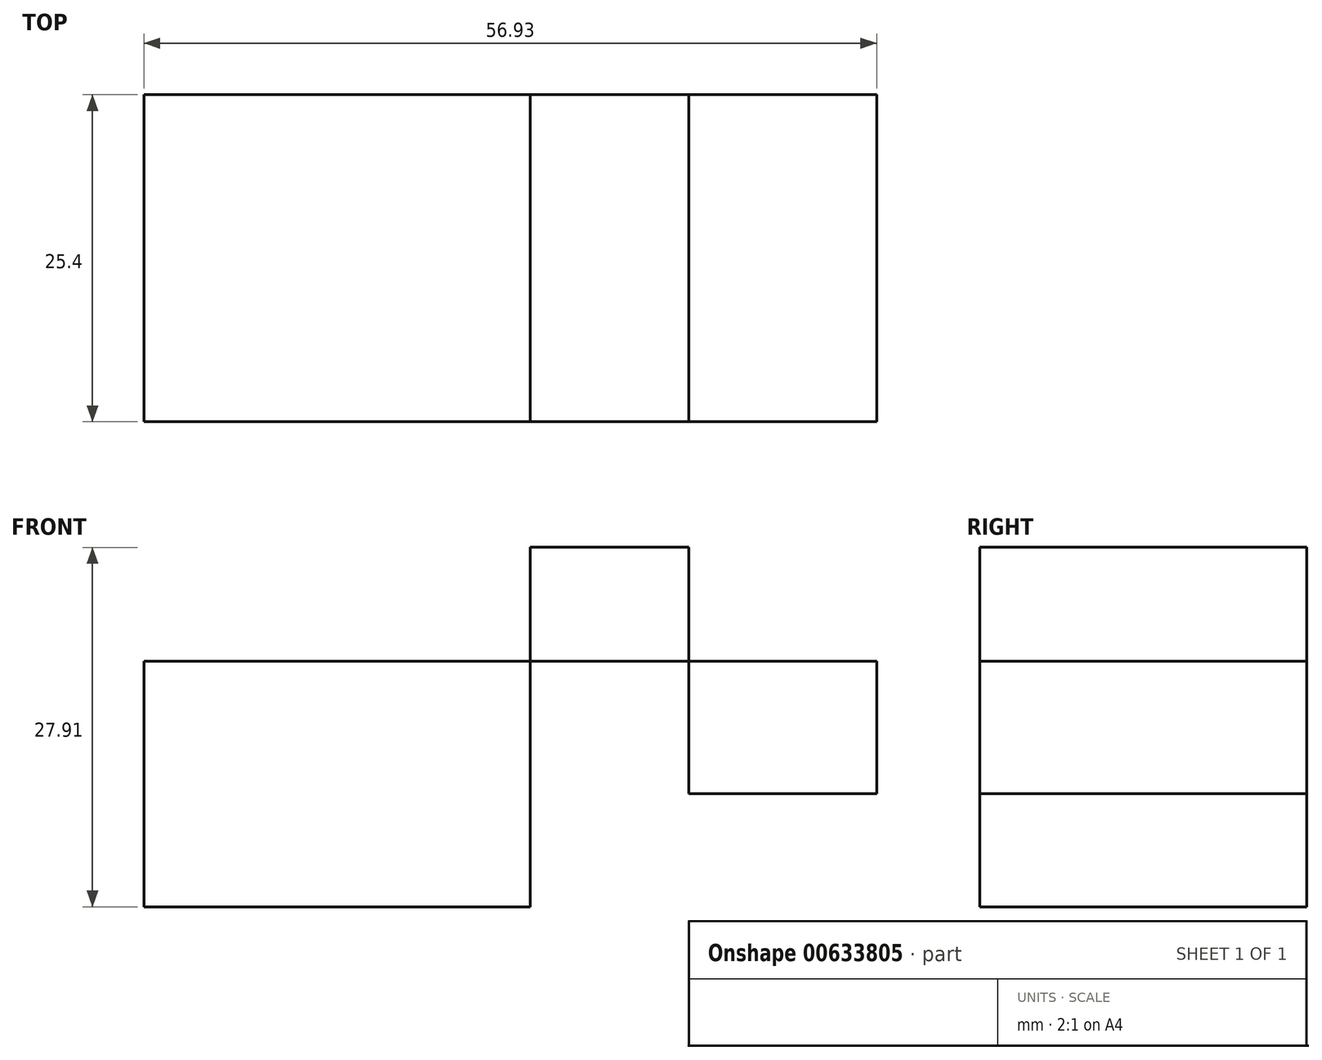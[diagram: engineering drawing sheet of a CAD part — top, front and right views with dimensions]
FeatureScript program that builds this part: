
annotation { "Feature Type Name" : "Feature", "Feature Type Description" : "" }
export const myFeature = defineFeature(function(context is Context, id is Id, definition is map)
    precondition{}
    {
        {
            var Q0;
            Q0=qCreatedBy(makeId("Front.planeOp"),FACE);
            var sketch = newSketch(context, id + "F0", { "sketchPlane" : qUnion([Q0])});
            skLineSegment(sketch, "E0.bottom", {"start": v(-30, 19.08) * mm, "end": v(0, 19.08) * mm});
            skLineSegment(sketch, "E0.top", {"start": v(-30, 0) * mm, "end": v(0, 0) * mm});
            skLineSegment(sketch, "E0.left", {"start": v(-30, 19.08) * mm, "end": v(-30, 0) * mm});
            skLineSegment(sketch, "E0.right", {"start": v(0, 19.08) * mm, "end": v(0, 0) * mm});
            skLineSegment(sketch, "E1.bottom", {"start": v(0, 19.08) * mm, "end": v(12.33, 19.08) * mm});
            skLineSegment(sketch, "E1.top", {"start": v(0, 27.91) * mm, "end": v(12.33, 27.91) * mm});
            skLineSegment(sketch, "E1.left", {"start": v(0, 19.08) * mm, "end": v(0, 27.91) * mm});
            skLineSegment(sketch, "E1.right", {"start": v(12.33, 19.08) * mm, "end": v(12.33, 27.91) * mm});
            skLineSegment(sketch, "E2.bottom", {"start": v(12.33, 19.08) * mm, "end": v(26.93, 19.08) * mm});
            skLineSegment(sketch, "E2.top", {"start": v(12.33, 8.77) * mm, "end": v(26.93, 8.77) * mm});
            skLineSegment(sketch, "E2.left", {"start": v(12.33, 19.08) * mm, "end": v(12.33, 8.77) * mm});
            skLineSegment(sketch, "E2.right", {"start": v(26.93, 19.08) * mm, "end": v(26.93, 8.77) * mm});
            skSolve(sketch);
        }
        {
            var Q0;
            Q0=makeQuery(id+"F0.imprint","IMPRINT",FACE,{"disambiguationData":[TD([[makeQuery(id+"F0.imprint","IMPRINT",EDGE,{"derivedFrom":sQuery(id+"F0.wireOp",EDGE,"E0.bottom")}),-1.0]])]});
            var Q1;
            Q1=makeQuery(id+"F0.imprint","IMPRINT",FACE,{"disambiguationData":[TD([[makeQuery(id+"F0.imprint","IMPRINT",EDGE,{"derivedFrom":sQuery(id+"F0.wireOp",EDGE,"E1.bottom")}),1.0]])]});
            var Q2;
            Q2=makeQuery(id+"F0.imprint","IMPRINT",FACE,{"disambiguationData":[TD([[makeQuery(id+"F0.imprint","IMPRINT",EDGE,{"derivedFrom":sQuery(id+"F0.wireOp",EDGE,"E2.bottom")}),-1.0]])]});
            extrude(context, id + "F1", {"entities" : qUnion([Q0, Q1, Q2]), "depth" : 25.4 * mm, "offsetDistance" : 25.4 * mm});
        }
    });
